# Revit family: NutriLED
name_source: partatom
category: Lighting Fixtures
revit_build: Autodesk Revit MEP 2012 (Build: 20110916_2132(x64)
units: mm (PartAtom-declared; Revit-internal decimal feet)

## types (2) — shared parameters
Apparent Load = 0 VA
Color Filter = 16777215
Cover Material = Black
Default Elevation = 48.000"
Description = LED Horticultural Light
Dimming Lamp Color Temperature Shift = <None>
Emit from Line Length = 24.000"
Glass = Glass
Lamp = LED
Manufacturer = Hubbell Industrial Lighting
Manufacturer Fax = 866-898-0131
Model = NutriLED
Nominal Watts = 62 W
Photometric Web File = 14.00782.IES
Product Documentation Link = http://www.hubbellindustrial.com
Product Material = Aluminum
Product Page URL = http://www.hubbellindustrial.com
Tilt Angle = -90.00°
URL = http://www.hubbellindustrial.com
Voltage = 120 V

## per-type parameters (varying)
| type | Length |
| NGL 24 | 50.000" |
| NGL 12 | 25.000" |

## geometry (parser evidence)
native form markers: Sweep x5
no freeform markers — native parametric forms only
